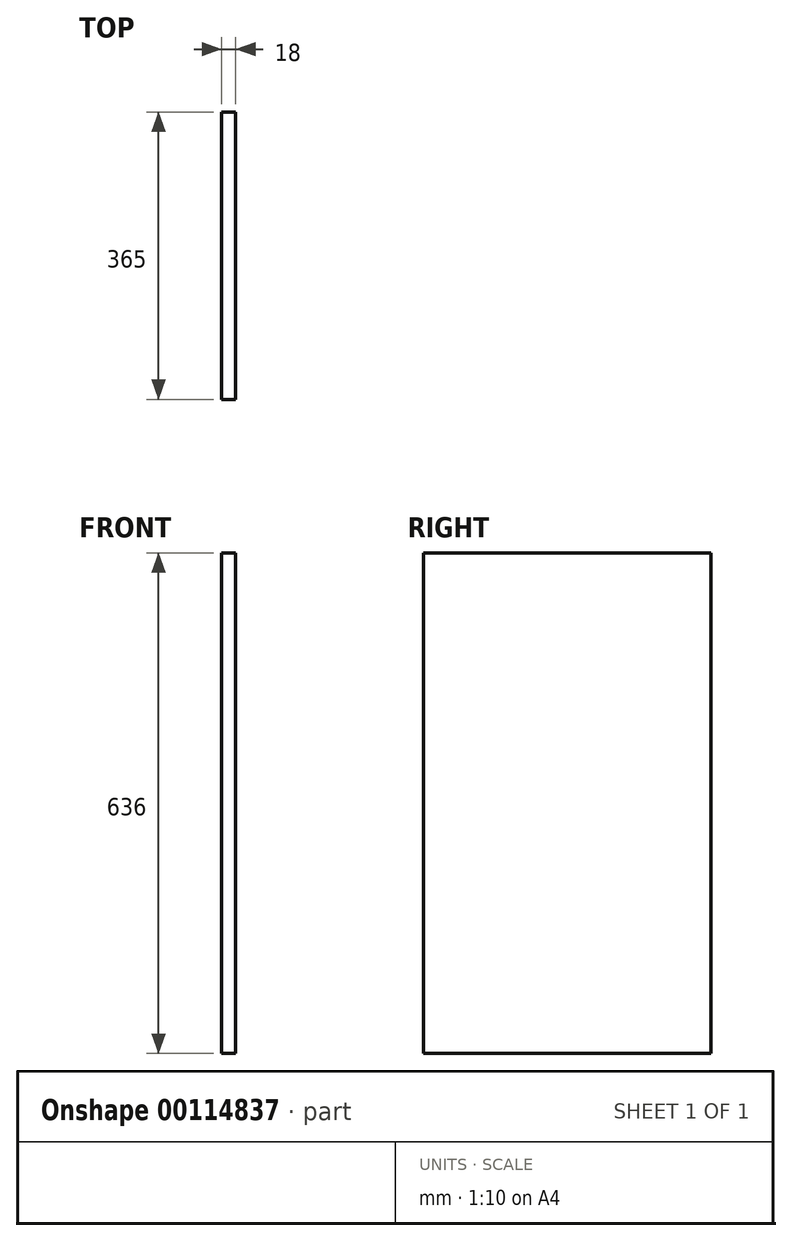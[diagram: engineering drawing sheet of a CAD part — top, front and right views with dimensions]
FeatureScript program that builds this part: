
annotation { "Feature Type Name" : "Feature", "Feature Type Description" : "" }
export const myFeature = defineFeature(function(context is Context, id is Id, definition is map)
    precondition{}
    {
        {
            var Q0;
            Q0=qCreatedBy(makeId("Right.planeOp"),FACE);
            var sketch = newSketch(context, id + "F0", { "sketchPlane" : qUnion([Q0])});
            skLineSegment(sketch, "E0.bottom", {"start": v(0, 0) * mm, "end": v(365, 0) * mm});
            skLineSegment(sketch, "E0.top", {"start": v(0, 636) * mm, "end": v(365, 636) * mm});
            skLineSegment(sketch, "E0.left", {"start": v(0, 0) * mm, "end": v(0, 636) * mm});
            skLineSegment(sketch, "E0.right", {"start": v(365, 0) * mm, "end": v(365, 636) * mm});
            skSolve(sketch);
        }
        {
            var Q0;
            Q0=makeQuery(id+"F0.imprint","IMPRINT",FACE,{"disambiguationData":[TD([[makeQuery(id+"F0.imprint","IMPRINT",EDGE,{"derivedFrom":sQuery(id+"F0.wireOp",EDGE,"E0.bottom")}),1.0]])]});
            extrude(context, id + "F1", {"entities" : qUnion([Q0]), "depth" : 18 * mm});
        }
    });
